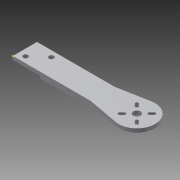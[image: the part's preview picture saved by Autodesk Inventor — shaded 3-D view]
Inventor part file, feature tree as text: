
AUTODESK INVENTOR PART (.ipt)
format: ipt  version: 2015 (Build 190159000, 159)  size: 151,552 bytes
history: native  units: mm
features: sketch x9, extrude x7, pattern_circular x1, fillet x1
ambient origin geometry x8: Origin, YZ Plane, XZ Plane, XY Plane, X Axis, Y Axis, Z Axis, Center Point
bodies: Solid1 (feature_tree)
feature tree (18):
  sketch  "Sketch1"  dims[d5=30.0mm d6=92.5mm]
  extrude  "Extrusion1"  Depth=92.5mm
  extrude  "Extrusion2"  Depth=3.0mm
  extrude  "Extrusion3"  Depth=2.6mm
  pattern_circular  "Circular Pattern1"  Count=4 Angle=360.0deg
  extrude  "Extrusion4"  Depth=20.0mm
  extrude  "Extrusion5"  Depth=10.0mm TaperAngle=0.0deg
  extrude  "Extrusion6"  Depth=4.064mm
  sketch  "Sketch7"  dims[d26=20.0mm d27=3.2mm]
  sketch  "Sketch8"  dims[d28=3.2mm d29=10.0mm d30=0.0mm]
  sketch  "Sketch9"  dims[d31=4.064mm d32=4.064mm]
  extrude  "Extrusion8"  Depth=2.0mm
  fillet  "Fillet2"  Radius=10.0mm
  sketch  "Sketch3"  dims[d7=3.0mm d8=0.0mm d9=3.0mm]
  sketch  "Sketch4"  dims[d10=10.0mm d11=0.0mm d18=2.6mm]
  sketch  "Sketch5"  dims[d19=2.6mm]
  sketch  "Sketch6"  dims[d21=10.0mm d22=0.0mm d23=40.0mm d24=360.0deg]
  sketch  "Sketch11"  dims[d33=10.0mm d34=0.0mm d35=6.1468mm d36=10.0mm d37=0.0mm d42=22.5mm d43=2.0mm d44=0.0mm d45=2.0mm]
